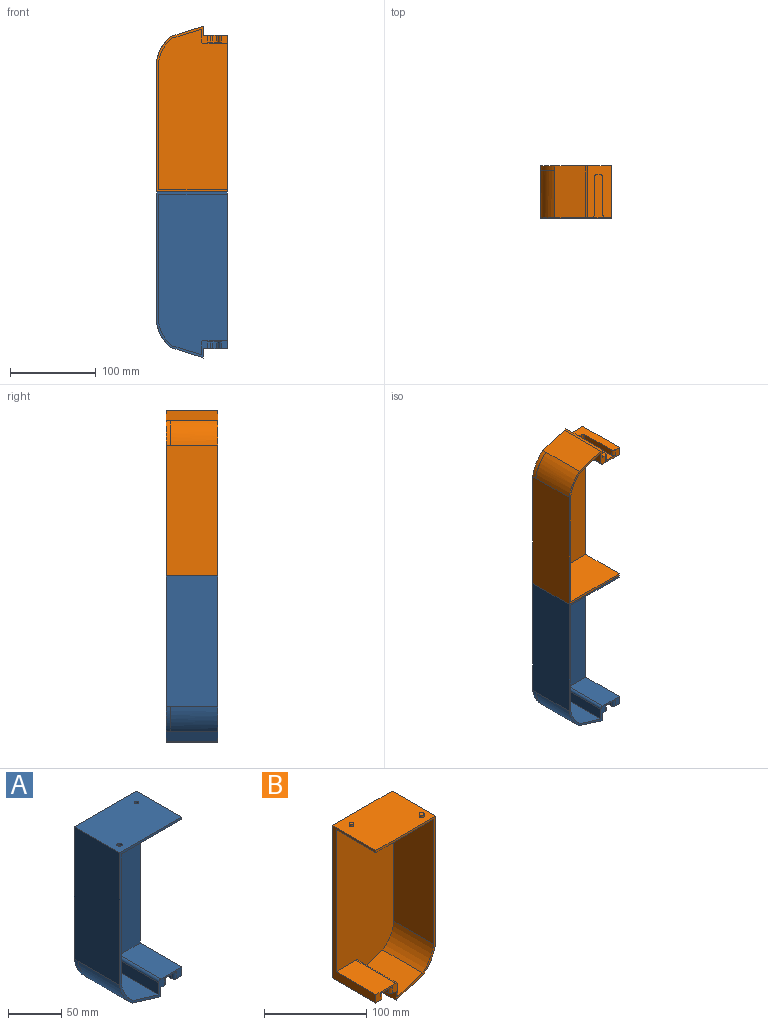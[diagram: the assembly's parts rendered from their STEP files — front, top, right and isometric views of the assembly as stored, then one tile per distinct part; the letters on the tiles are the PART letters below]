
ASSEMBLY  parts=2 mates=1
PART A: 30 faces, bbox 82.5x60x193.2 mm
  f0: plane 186.91x80mm, normal (0,-1,0), area 13953.3mm2, adj f6,f15,f16,f17,f18,f19,f20,f29
  f1: plane 60x2.5mm, normal (-0.33,0,-0.94), area 159.2mm2, adj f2,f11,f12,f21
  f2: plane 60x35.38mm, normal (-0.3,0,-0.95), area 2225.1mm2, adj f1,f3,f12,f14,f21
  f3: cylinder r=45.29mm len=28.85mm, axis (0,1,0), area 170.7mm2, adj f2,f4,f12,f13
  f4: plane 152.34x60mm, normal (-1,0,0), area 9140.2mm2, adj f3,f5,f12,f14,f21
  f5: plane 82.5x60mm, normal (0,0,1), area 4916.3mm2, adj f4,f6,f12,f21,f23,f24
  f6: plane 182.5x60mm, normal (1,0,0), area 1600mm2, adj f0,f5,f10,f12,f15,f20,f21
  f7: plane 44x8mm, normal (-1,0,0), area 352mm2, adj f8,f10,f25,f26
  f8: plane 50x16mm, normal (0,0,-1), area 500mm2, adj f7,f9,f21,f22,f25,f26,f27,f28
  f9: plane 44x8mm, normal (1,0,0), area 352mm2, adj f8,f10,f27,f28
  f10: plane 60x27.9mm, normal (0,0,-1), area 1173.7mm2, adj f6,f7,f9,f11,f12,f21,f22,f25
  f11: plane 60x10.7mm, normal (1,0,0), area 642.1mm2, adj f1,f10,f12,f21
  f12: plane 193.2x82.5mm, normal (0,1,0), area 15040mm2, adj f1,f2,f3,f4,f5,f6,f10,f11
  f13: plane 28.85x16.73mm, normal (0,-1,0), area 0.6mm2, adj f3,f14
  f14: cylinder r=45.64mm len=55mm, axis (0,1,0), area 1877.5mm2, adj f2,f4,f13,f21
  f15: plane 80x55mm, normal (0,0,-1), area 4366.3mm2, adj f0,f6,f16,f21,f23,f24
  f16: plane 149.65x55mm, normal (1,0,0), area 8230.6mm2, adj f0,f15,f17,f21
  f17: cylinder r=42.79mm len=55mm, axis (0,1,0), area 1737.1mm2, adj f0,f16,f18,f21
  f18: plane 55x34.22mm, normal (0.29,0,0.96), area 1968.5mm2, adj f0,f17,f19,f21
  f19: plane 55x13.91mm, normal (-1,0,0), area 765.1mm2, adj f0,f18,f21,f29
  f20: plane 55x27.4mm, normal (0,0,1), area 1506.7mm2, adj f0,f6,f21,f29
  f21: plane 193.2x82.5mm, normal (0,-1,0), area 958.1mm2, adj f1,f2,f4,f5,f6,f8,f10,f11
  f22: plane 8x4mm, normal (0,-1,0), area 32mm2, adj f8,f10,f25,f28
  f23: cylinder r=2.12mm len=4.23mm, axis (0,0,1), area 33.2mm2, adj f5,f15
  f24: cylinder r=2.5mm len=5mm, axis (0,0,1), area 39.3mm2, adj f5,f15
  f25: cylinder r=3mm len=8mm, axis (0,0,1), area 37.7mm2, adj f7,f8,f10,f22
  f26: cylinder r=3mm len=8mm, axis (0,0,-1), area 37.7mm2, adj f7,f8,f10,f21
  f27: cylinder r=3mm len=8mm, axis (0,0,1), area 37.7mm2, adj f8,f9,f10,f21
  f28: cylinder r=3mm len=8mm, axis (0,0,-1), area 37.7mm2, adj f8,f9,f10,f22
  f29: cylinder r=3mm len=55mm, axis (0,-1,0), area 259.2mm2, adj f0,f19,f20,f21
PART B: 32 faces, bbox 82.5x60x195.7 mm
  f0: plane 186.91x80mm, normal (0,-1,0), area 13953.3mm2, adj f6,f15,f16,f17,f18,f19,f20,f29
  f1: plane 60x2.5mm, normal (0.33,0,-0.94), area 159.2mm2, adj f2,f11,f12,f21
  f2: plane 60x35.38mm, normal (0.3,0,-0.95), area 2225.1mm2, adj f1,f3,f12,f14,f21
  f3: cylinder r=45.29mm len=28.85mm, axis (0,1,0), area 170.7mm2, adj f2,f4,f12,f13
  f4: plane 152.34x60mm, normal (1,0,0), area 9140.2mm2, adj f3,f5,f12,f14,f21
  f5: plane 82.5x60mm, normal (0,0,1), area 4916.3mm2, adj f4,f6,f12,f21,f23,f25
  f6: plane 182.5x60mm, normal (-1,0,0), area 1600mm2, adj f0,f5,f10,f12,f15,f20,f21
  f7: plane 44x8mm, normal (1,0,0), area 352mm2, adj f8,f10,f28,f31
  f8: plane 50x16mm, normal (0,0,-1), area 500mm2, adj f7,f9,f21,f22,f27,f28,f30,f31
  f9: plane 44x8mm, normal (-1,0,0), area 352mm2, adj f8,f10,f27,f30
  f10: plane 60x27.9mm, normal (0,0,-1), area 1173.7mm2, adj f6,f7,f9,f11,f12,f21,f22,f27
  f11: plane 60x10.7mm, normal (-1,0,0), area 642.1mm2, adj f1,f10,f12,f21
  f12: plane 193.2x82.5mm, normal (0,1,0), area 15040mm2, adj f1,f2,f3,f4,f5,f6,f10,f11
  f13: plane 28.85x16.73mm, normal (0,-1,0), area 0.6mm2, adj f3,f14
  f14: cylinder r=45.64mm len=55mm, axis (0,1,0), area 1877.5mm2, adj f2,f4,f13,f21
  f15: plane 80x55mm, normal (0,0,-1), area 4400mm2, adj f0,f6,f16,f21
  f16: plane 149.65x55mm, normal (-1,0,0), area 8230.6mm2, adj f0,f15,f17,f21
  f17: cylinder r=42.79mm len=55mm, axis (0,1,0), area 1737.1mm2, adj f0,f16,f18,f21
  f18: plane 55x34.22mm, normal (-0.29,0,0.96), area 1968.5mm2, adj f0,f17,f19,f21
  f19: plane 55x13.91mm, normal (1,0,0), area 765.1mm2, adj f0,f18,f21,f29
  f20: plane 55x27.4mm, normal (0,0,1), area 1506.7mm2, adj f0,f6,f21,f29
  f21: plane 193.2x82.5mm, normal (0,-1,0), area 958.1mm2, adj f1,f2,f4,f5,f6,f8,f10,f11
  f22: plane 8x4mm, normal (0,-1,0), area 32mm2, adj f8,f10,f27,f28
  f23: cylinder r=2.5mm len=5mm, axis (0,0,-1), area 39.3mm2, adj f5,f24
  f24: plane 5x5mm, normal (0,0,1), area 19.6mm2, adj f23
  f25: cylinder r=2.12mm len=4.23mm, axis (0,0,-1), area 33.2mm2, adj f5,f26
  f26: plane 4.23x4.23mm, normal (0,0,1), area 14.1mm2, adj f25
  f27: cylinder r=3mm len=8mm, axis (0,0,-1), area 37.7mm2, adj f8,f9,f10,f22
  f28: cylinder r=3mm len=8mm, axis (0,0,1), area 37.7mm2, adj f7,f8,f10,f22
  f29: cylinder r=3mm len=55mm, axis (0,-1,0), area 259.2mm2, adj f0,f19,f20,f21
  f30: cylinder r=3mm len=8mm, axis (0,0,1), area 37.7mm2, adj f8,f9,f10,f21
  f31: cylinder r=3mm len=8mm, axis (0,0,-1), area 37.7mm2, adj f7,f8,f10,f21
PLACE A t=(-61.58,-45.38,-22.65)mm
PLACE B rot(axis=(0,-1,0),180deg) t=(-64.08,-45.38,564.51)mm
MATE fastened B.f23 <-> A.f24  axis (0,0,-1) through (-54.58,-95.88,379.51)mm
